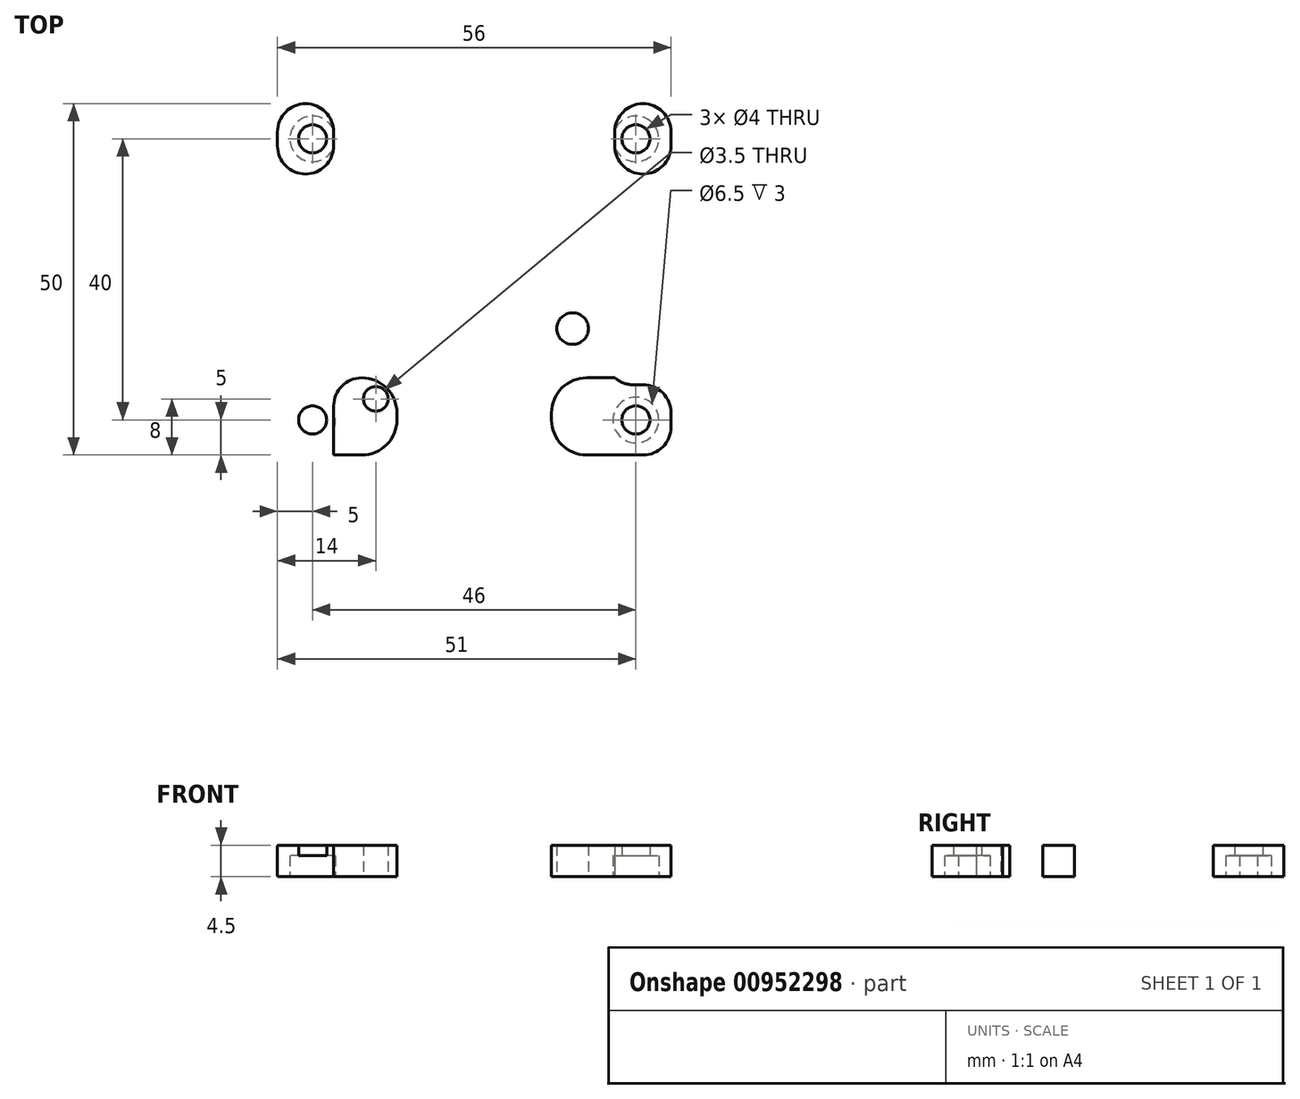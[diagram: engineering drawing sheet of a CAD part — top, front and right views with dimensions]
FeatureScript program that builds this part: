
annotation { "Feature Type Name" : "Feature", "Feature Type Description" : "" }
export const myFeature = defineFeature(function(context is Context, id is Id, definition is map)
    precondition{}
    {
        {
            var Q0;
            Q0=qCreatedBy(makeId("Top.planeOp"),FACE);
            var sketch = newSketch(context, id + "F0", { "sketchPlane" : qUnion([Q0])});
            skLineSegment(sketch, "E0.bottom", {"start": v(20, -27) * mm, "end": v(-20, -27) * mm});
            skLineSegment(sketch, "E0.top", {"start": v(20, 27) * mm, "end": v(-20, 27) * mm});
            skLineSegment(sketch, "E0.left", {"start": v(20, -27) * mm, "end": v(20, 27) * mm});
            skLineSegment(sketch, "E0.right", {"start": v(-20, -27) * mm, "end": v(-20, 27) * mm});
            skPoint(sketch, "E0.middle", {"position": v(0, 0) * mm});
            skCircle(sketch, "E1", {"center": v(0, 8.9) * mm, "radius": 6 * mm});
            skCircle(sketch, "E2", {"center": v(14, 20) * mm, "radius": 2.25 * mm});
            skCircle(sketch, "E3.MirrorC", {"center": v(-14, 20) * mm, "radius": 2.25 * mm});
            skCircle(sketch, "E4.MirrorC", {"center": v(14, -20) * mm, "radius": 2.25 * mm});
            skCircle(sketch, "E5.MirrorC", {"center": v(-14, -20) * mm, "radius": 2.25 * mm});
            skCircle(sketch, "E6", {"center": v(-14, -10) * mm, "radius": 1.75 * mm});
            skCircle(sketch, "E7.MirrorC", {"center": v(14, -10) * mm, "radius": 1.75 * mm});
            skLineSegment(sketch, "E8.bottom", {"start": v(-20, -27) * mm, "end": v(20, -27) * mm});
            skLineSegment(sketch, "E8.top", {"start": v(-20, -38) * mm, "end": v(-11, -38) * mm});
            skLineSegment(sketch, "E8.left", {"start": v(-20, -27) * mm, "end": v(-20, -38) * mm});
            skLineSegment(sketch, "E8.right", {"start": v(20, -27) * mm, "end": v(20, -38) * mm});
            skCircle(sketch, "E9", {"center": v(-14, -30) * mm, "radius": 1.75 * mm});
            skCircle(sketch, "E10.MirrorC", {"center": v(14, -30) * mm, "radius": 1.75 * mm});
            skLineSegment(sketch, "E11.MirrorCS", {"start": v(-28, 12) * mm, "end": v(-28, -38) * mm});
            skLineSegment(sketch, "E12.MirrorCS", {"start": v(-11, -38) * mm, "end": v(-28, -38) * mm});
            skLineSegment(sketch, "E13", {"start": v(-28, 12) * mm, "end": v(-20, 12) * mm});
            skLineSegment(sketch, "E14.left", {"start": v(-11, -38) * mm, "end": v(-11, -30) * mm});
            skLineSegment(sketch, "E14.right", {"start": v(11, -38) * mm, "end": v(11, -30) * mm});
            skLineSegment(sketch, "E15.top", {"start": v(-11, -27) * mm, "end": v(11, -27) * mm});
            skLineSegment(sketch, "E15.left", {"start": v(-11, -30) * mm, "end": v(-11, -27) * mm});
            skLineSegment(sketch, "E15.right", {"start": v(11, -30) * mm, "end": v(11, -27) * mm});
            skCircle(sketch, "E16", {"center": v(0, -15) * mm, "radius": 7.5 * mm});
            skLineSegment(sketch, "E17.MirrorCS", {"start": v(-28, 2) * mm, "end": v(-20, 2) * mm});
            skCircle(sketch, "E18.MirrorC", {"center": v(-23, 7) * mm, "radius": 2 * mm});
            skCircle(sketch, "E19.MirrorC", {"center": v(-23, -33) * mm, "radius": 2 * mm});
            skLineSegment(sketch, "E20", {"start": v(-28, -28) * mm, "end": v(-20, -28) * mm});
            skPoint(sketch, "E21.MirrorCS.start.orphan", {"position": v(-20, 27) * mm});
            skLineSegment(sketch, "E22.MirrorCS", {"start": v(28, 12) * mm, "end": v(20, 12) * mm});
            skCircle(sketch, "E23.MirrorC", {"center": v(23, 7) * mm, "radius": 2 * mm});
            skLineSegment(sketch, "E24.MirrorCS", {"start": v(28, 12) * mm, "end": v(28, -38) * mm});
            skLineSegment(sketch, "E25.MirrorCS", {"start": v(28, 2) * mm, "end": v(20, 2) * mm});
            skLineSegment(sketch, "E26.MirrorCS", {"start": v(28, -28) * mm, "end": v(20, -28) * mm});
            skLineSegment(sketch, "E27.MirrorCS", {"start": v(11, -38) * mm, "end": v(28, -38) * mm});
            skCircle(sketch, "E28.MirrorC", {"center": v(23, -33) * mm, "radius": 2 * mm});
            skLineSegment(sketch, "E29.trimOffspring", {"start": v(11, -38) * mm, "end": v(20, -38) * mm});
            skSolve(sketch);
        }
        {
            var Q0;
            Q0=makeQuery(id+"F0.imprint","IMPRINT",FACE,{"disambiguationData":[TD([[makeQuery(id+"F0.imprint","IMPRINT",EDGE,{"derivedFrom":sQuery(id+"F0.wireOp",EDGE,"EJkg02S6-5hP4-Ptk8-ohYH-sUQTjE6RF98o")}),-1.0]])]});
            var Q1;
            Q1=makeQuery(id+"F0.imprint","IMPRINT",FACE,{"disambiguationData":[TD([[makeQuery(id+"F0.imprint","IMPRINT",EDGE,{"derivedFrom":sQuery(id+"F0.wireOp",EDGE,"fef3ff0a-59c7-4115-b365-545473ce19e80.MirrorC")}),-1.0]])]});
            var Q2;
            Q2=makeQuery(id+"F0.imprint","IMPRINT",FACE,{"disambiguationData":[TD([[makeQuery(id+"F0.imprint","IMPRINT",EDGE,{"derivedFrom":sQuery(id+"F0.wireOp",EDGE,"83bcec90-f7c3-4e6e-a305-b15cb3412ae00.MirrorC")}),1.0]])]});
            var Q3;
            {var subQ3=sQuery(id+"F0.wireOp",EDGE,"E8.bottom");Q3=makeQuery(id+"F0.imprint","IMPRINT",FACE,{"disambiguationData":[TD([[makeQuery(id+"F0.imprint","IMPRINT",EDGE,{"derivedFrom":subQ3}),-1.0]])]});}
            var Q4;
            Q4=makeQuery(id+"F0.imprint","IMPRINT",FACE,{"disambiguationData":[TD([[makeQuery(id+"F0.imprint","IMPRINT",EDGE,{"derivedFrom":sQuery(id+"F0.wireOp",EDGE,"E1")}),-1.0]])]});
            var Q5;
            {var subQ4=sQuery(id+"F0.wireOp",EDGE,"cf22b2a7-dd2e-4435-8f2e-39b4c899264f0.MirrorCS");Q5=makeQuery(id+"F0.imprint","IMPRINT",FACE,{"disambiguationData":[TD([[makeQuery(id+"F0.imprint","IMPRINT",EDGE,{"derivedFrom":subQ4}),-1.0]])]});}
            var Q6;
            {var subQ1=sQuery(id+"F0.wireOp",EDGE,"E0.top");Q6=makeQuery(id+"F0.imprint","IMPRINT",FACE,{"disambiguationData":[TD([[makeQuery(id+"F0.imprint","IMPRINT",EDGE,{"derivedFrom":subQ1}),1.0]])]});}
            var Q7;
            Q7=makeQuery(id+"F0.imprint","IMPRINT",FACE,{"disambiguationData":[TD([[makeQuery(id+"F0.imprint","IMPRINT",EDGE,{"derivedFrom":sQuery(id+"F0.wireOp",EDGE,"E9")}),-1.0]])]});
            var Q8;
            Q8=makeQuery(id+"F0.imprint","IMPRINT",FACE,{"disambiguationData":[TD([[makeQuery(id+"F0.imprint","IMPRINT",EDGE,{"derivedFrom":sQuery(id+"F0.wireOp",EDGE,"E10.MirrorC")}),1.0]])]});
            var Q9;
            {var subQ6=sQuery(id+"F0.wireOp",EDGE,"E14.left");Q9=makeQuery(id+"F0.imprint","IMPRINT",FACE,{"disambiguationData":[TD([[makeQuery(id+"F0.imprint","IMPRINT",EDGE,{"derivedFrom":subQ6}),1.0]])]});}
            var Q10;
            {var subQ10=sQuery(id+"F0.wireOp",EDGE,"E14.right");Q10=makeQuery(id+"F0.imprint","IMPRINT",FACE,{"disambiguationData":[TD([[makeQuery(id+"F0.imprint","IMPRINT",EDGE,{"derivedFrom":subQ10}),-1.0]])]});}
            var Q11;
            Q11=makeQuery(id+"F0.imprint","IMPRINT",FACE,{"disambiguationData":[TD([[makeQuery(id+"F0.imprint","IMPRINT",EDGE,{"derivedFrom":sQuery(id+"F0.wireOp",EDGE,"E4.MirrorC")}),1.0]])]});
            var Q12;
            {var subQ0=sQuery(id+"F0.wireOp",EDGE,"ed930464-472b-4d13-baf5-ac3ff7af2bd40.MirrorCS");Q12=makeQuery(id+"F0.imprint","IMPRINT",FACE,{"disambiguationData":[TD([[makeQuery(id+"F0.imprint","IMPRINT",EDGE,{"derivedFrom":subQ0}),1.0]])]});}
            var Q13;
            {var subQ1=sQuery(id+"F0.wireOp",EDGE,"E13");Q13=makeQuery(id+"F0.imprint","IMPRINT",FACE,{"disambiguationData":[TD([[makeQuery(id+"F0.imprint","IMPRINT",EDGE,{"derivedFrom":subQ1}),-1.0]])]});}
            var Q14;
            {var subQ1=sQuery(id+"F0.wireOp",EDGE,"D3Rt8Xrc-2Lu0-yaOw-90uC-Wp8pwz9pcPP1.top");Q14=makeQuery(id+"F0.imprint","IMPRINT",FACE,{"disambiguationData":[TD([[makeQuery(id+"F0.imprint","IMPRINT",EDGE,{"derivedFrom":subQ1}),1.0]])]});}
            var Q15;
            {var subQ1=sQuery(id+"F0.wireOp",EDGE,"E22.MirrorCS");Q15=makeQuery(id+"F0.imprint","IMPRINT",FACE,{"disambiguationData":[TD([[makeQuery(id+"F0.imprint","IMPRINT",EDGE,{"derivedFrom":subQ1}),1.0]])]});}
            var Q16;
            {var subQ1=sQuery(id+"F0.wireOp",EDGE,"E26.MirrorCS");Q16=makeQuery(id+"F0.imprint","IMPRINT",FACE,{"disambiguationData":[TD([[makeQuery(id+"F0.imprint","IMPRINT",EDGE,{"derivedFrom":subQ1}),1.0]])]});}
            var Q17;
            Q17=makeQuery(id+"F0.imprint","IMPRINT",FACE,{"disambiguationData":[TD([[makeQuery(id+"F0.imprint","IMPRINT",EDGE,{"derivedFrom":sQuery(id+"F0.wireOp",EDGE,"E19.MirrorC")}),1.0]])]});
            extrude(context, id + "F1", {"entities" : qUnion([Q0, Q1, Q2, Q3, Q4, Q5, Q6, Q7, Q8, Q9, Q10, Q11, Q12, Q13, Q14, Q15, Q16, Q17]), "depth" : 4.5 * mm, "offsetDistance" : 25 * mm});
        }
        {
            var Q0;
            Q0=makeQuery(id+"F1.opExtrude","CAP_FACE",FACE,{"disambiguationData":[OSD([sQuery(id+"F0.wireOp",EDGE,"E0.bottom"),sQuery(id+"F0.wireOp",EDGE,"E0.top"),sQuery(id+"F0.wireOp",EDGE,"E0.left"),sQuery(id+"F0.wireOp",EDGE,"E0.right"),sQuery(id+"F0.wireOp",EDGE,"E1"),sQuery(id+"F0.wireOp",EDGE,"E2"),sQuery(id+"F0.wireOp",EDGE,"E3.MirrorC"),sQuery(id+"F0.wireOp",EDGE,"E4.MirrorC"),sQuery(id+"F0.wireOp",EDGE,"E5.MirrorC")])],"isStart":false});
            var sketch = newSketch(context, id + "F2", { "sketchPlane" : qUnion([Q0])});
            skCircle(sketch, "E30", {"center": v(0, 20.9) * mm, "radius": 1.3 * mm});
            skCircle(sketch, "E31.1.0", {"center": v(-8.49, 17.39) * mm, "radius": 1.3 * mm});
            skCircle(sketch, "E31.2.0", {"center": v(-12, 8.9) * mm, "radius": 1.3 * mm});
            skCircle(sketch, "E31.3.0", {"center": v(-8.49, 0.41) * mm, "radius": 1.3 * mm});
            skCircle(sketch, "E31.4.0", {"center": v(0, -3.1) * mm, "radius": 1.3 * mm});
            skCircle(sketch, "E31.5.0", {"center": v(8.49, 0.41) * mm, "radius": 1.3 * mm});
            skCircle(sketch, "E31.6.0", {"center": v(12, 8.9) * mm, "radius": 1.3 * mm});
            skCircle(sketch, "E31.7.0", {"center": v(8.49, 17.39) * mm, "radius": 1.3 * mm});
            skPoint(sketch, "E31.center", {"position": v(0, 8.9) * mm});
            skSolve(sketch);
        }
        {
            var Q0;
            Q0 = qSketchRegion(id + "F2", true);
            extrude(context, id + "F3", {"entities" : qUnion([Q0]), "operationType" : NewBodyOperationType.REMOVE, "oppositeDirection" : true, "depth" : 25 * mm, "offsetDistance" : 25 * mm});
        }
        {
            var Q0;
            Q0=makeQuery(id+"F1.opExtrude","CAP_FACE",FACE,{"disambiguationData":[OSD([sQuery(id+"F0.wireOp",EDGE,"E0.bottom"),sQuery(id+"F0.wireOp",EDGE,"E0.top"),sQuery(id+"F0.wireOp",EDGE,"E0.left"),sQuery(id+"F0.wireOp",EDGE,"E0.right"),sQuery(id+"F0.wireOp",EDGE,"E1"),sQuery(id+"F0.wireOp",EDGE,"E2"),sQuery(id+"F0.wireOp",EDGE,"E3.MirrorC"),sQuery(id+"F0.wireOp",EDGE,"E4.MirrorC"),sQuery(id+"F0.wireOp",EDGE,"E5.MirrorC"),sQuery(id+"F0.wireOp",EDGE,"E6"),sQuery(id+"F0.wireOp",EDGE,"E7.MirrorC")])],"isStart":false});
            var sketch = newSketch(context, id + "F4", { "sketchPlane" : qUnion([Q0])});
            skCircle(sketch, "E32", {"center": v(0, 8.9) * mm, "radius": 9.25 * mm});
            skSolve(sketch);
        }
        {
            var Q0;
            Q0=makeQuery(id+"F4.imprint","IMPRINT",FACE,{"disambiguationData":[TD([[makeQuery(id+"F4.imprint","IMPRINT",EDGE,{"derivedFrom":sQuery(id+"F4.wireOp",EDGE,"E32")}),1.0]])]});
            extrude(context, id + "F5", {"entities" : qUnion([Q0]), "operationType" : NewBodyOperationType.REMOVE, "oppositeDirection" : true, "depth" : 3 * mm, "offsetDistance" : 25 * mm});
        }
        {
            var Q0;
            Q0=makeQuery(id+"F1.opExtrude","SWEPT_EDGE",EDGE,{"disambiguationData":[OSD([sQuery(id+"F0.wireOp",EDGE,"D3Rt8Xrc-2Lu0-yaOw-90uC-Wp8pwz9pcPP1.bottom"),sQuery(id+"F0.wireOp",EDGE,"D3Rt8Xrc-2Lu0-yaOw-90uC-Wp8pwz9pcPP1.right")])]});
            var Q1;
            Q1=makeQuery(id+"F1.opExtrude","SWEPT_EDGE",EDGE,{"disambiguationData":[OSD([sQuery(id+"F0.wireOp",EDGE,"E21.MirrorCS"),sQuery(id+"F0.wireOp",EDGE,"E11.MirrorCS")])]});
            var Q2;
            Q2=makeQuery(id+"F1.opExtrude","SWEPT_EDGE",EDGE,{"disambiguationData":[OSD([sQuery(id+"F0.wireOp",EDGE,"E11.MirrorCS"),sQuery(id+"F0.wireOp",EDGE,"E12.MirrorCS")])]});
            var Q3;
            Q3=makeQuery(id+"F1.opExtrude","SWEPT_EDGE",EDGE,{"disambiguationData":[OSD([sQuery(id+"F0.wireOp",EDGE,"D3Rt8Xrc-2Lu0-yaOw-90uC-Wp8pwz9pcPP1.top"),sQuery(id+"F0.wireOp",EDGE,"D3Rt8Xrc-2Lu0-yaOw-90uC-Wp8pwz9pcPP1.right")])]});
            var Q4;
            Q4=makeQuery(id+"F1.opExtrude","SWEPT_EDGE",EDGE,{"disambiguationData":[OSD([sQuery(id+"F0.wireOp",EDGE,"E22.MirrorCS"),sQuery(id+"F0.wireOp",EDGE,"E24.MirrorCS")])]});
            var Q5;
            Q5=makeQuery(id+"F1.opExtrude","SWEPT_EDGE",EDGE,{"disambiguationData":[OSD([sQuery(id+"F0.wireOp",EDGE,"E24.MirrorCS"),sQuery(id+"F0.wireOp",EDGE,"E26.MirrorCS")])]});
            var Q6;
            Q6=makeQuery(id+"F1.opExtrude","SWEPT_EDGE",EDGE,{"disambiguationData":[OSD([sQuery(id+"F0.wireOp",EDGE,"E24.MirrorCS"),sQuery(id+"F0.wireOp",EDGE,"E27.MirrorCS")])]});
            var Q7;
            Q7=makeQuery(id+"F1.opExtrude","SWEPT_EDGE",EDGE,{"disambiguationData":[OSD([sQuery(id+"F0.wireOp",EDGE,"E0.right"),sQuery(id+"F0.wireOp",EDGE,"E17.MirrorCS")])]});
            var Q8;
            Q8=makeQuery(id+"F1.opExtrude","SWEPT_EDGE",EDGE,{"disambiguationData":[OSD([sQuery(id+"F0.wireOp",EDGE,"E0.right"),sQuery(id+"F0.wireOp",EDGE,"E8.bottom"),sQuery(id+"F0.wireOp",EDGE,"E8.left"),sQuery(id+"F0.wireOp",EDGE,"E20")])]});
            var Q9;
            Q9=makeQuery(id+"F1.opExtrude","SWEPT_EDGE",EDGE,{"disambiguationData":[OSD([sQuery(id+"F0.wireOp",EDGE,"E24.MirrorCS"),sQuery(id+"F0.wireOp",EDGE,"E25.MirrorCS")])]});
            var Q10;
            Q10=makeQuery(id+"F1.opExtrude","SWEPT_EDGE",EDGE,{"disambiguationData":[OSD([sQuery(id+"F0.wireOp",EDGE,"D3Rt8Xrc-2Lu0-yaOw-90uC-Wp8pwz9pcPP1.left"),sQuery(id+"F0.wireOp",EDGE,"E25.MirrorCS")])]});
            var Q11;
            Q11=makeQuery(id+"F1.opExtrude","SWEPT_EDGE",EDGE,{"disambiguationData":[OSD([sQuery(id+"F0.wireOp",EDGE,"D3Rt8Xrc-2Lu0-yaOw-90uC-Wp8pwz9pcPP1.left"),sQuery(id+"F0.wireOp",EDGE,"E22.MirrorCS")])]});
            var Q12;
            Q12=makeQuery(id+"F1.opExtrude","SWEPT_EDGE",EDGE,{"disambiguationData":[OSD([sQuery(id+"F0.wireOp",EDGE,"E8.bottom"),sQuery(id+"F0.wireOp",EDGE,"D3Rt8Xrc-2Lu0-yaOw-90uC-Wp8pwz9pcPP1.left"),sQuery(id+"F0.wireOp",EDGE,"E26.MirrorCS")])]});
            var Q13;
            Q13=makeQuery(id+"F1.opExtrude","SWEPT_EDGE",EDGE,{"disambiguationData":[OSD([sQuery(id+"F0.wireOp",EDGE,"E0.top"),sQuery(id+"F0.wireOp",EDGE,"D3Rt8Xrc-2Lu0-yaOw-90uC-Wp8pwz9pcPP1.left")])]});
            var Q14;
            Q14=makeQuery(id+"F1.opExtrude","SWEPT_EDGE",EDGE,{"disambiguationData":[OSD([sQuery(id+"F0.wireOp",EDGE,"E0.top"),sQuery(id+"F0.wireOp",EDGE,"E0.right")])]});
            var Q15;
            Q15=makeQuery(id+"F1.opExtrude","SWEPT_EDGE",EDGE,{"disambiguationData":[OSD([sQuery(id+"F0.wireOp",EDGE,"E0.right"),sQuery(id+"F0.wireOp",EDGE,"E13")])]});
            fillet(context, id + "F6", {"entities" : qUnion([Q0, Q1, Q2, Q3, Q4, Q5, Q6, Q7, Q8, Q9, Q10, Q11, Q12, Q13, Q14, Q15]), "radius" : 4 * mm, "tangentPropagation" : true, "defaultsChanged" : true, "vertexSettings" : [], "allowEdgeOverflow" : false});
        }
        {
            var Q0;
            Q0=makeQuery(id+"F1.opExtrude","CAP_FACE",FACE,{"disambiguationData":[OSD([sQuery(id+"F0.wireOp",EDGE,"E0.top"),sQuery(id+"F0.wireOp",EDGE,"E0.right"),sQuery(id+"F0.wireOp",EDGE,"E1"),sQuery(id+"F0.wireOp",EDGE,"E2"),sQuery(id+"F0.wireOp",EDGE,"E3.MirrorC"),sQuery(id+"F0.wireOp",EDGE,"E4.MirrorC"),sQuery(id+"F0.wireOp",EDGE,"E5.MirrorC"),sQuery(id+"F0.wireOp",EDGE,"E6"),sQuery(id+"F0.wireOp",EDGE,"E7.MirrorC"),sQuery(id+"F0.wireOp",EDGE,"E8.top"),sQuery(id+"F0.wireOp",EDGE,"E8.left"),sQuery(id+"F0.wireOp",EDGE,"E9"),sQuery(id+"F0.wireOp",EDGE,"E10.MirrorC"),sQuery(id+"F0.wireOp",EDGE,"D3Rt8Xrc-2Lu0-yaOw-90uC-Wp8pwz9pcPP1.left"),sQuery(id+"F0.wireOp",EDGE,"D3Rt8Xrc-2Lu0-yaOw-90uC-Wp8pwz9pcPP1.right"),sQuery(id+"F0.wireOp",EDGE,"E11.MirrorCS"),sQuery(id+"F0.wireOp",EDGE,"54b7e0aa-d997-4b68-9832-fdfdaffa90230.MirrorC"),sQuery(id+"F0.wireOp",EDGE,"E13"),sQuery(id+"F0.wireOp",EDGE,"ed930464-472b-4d13-baf5-ac3ff7af2bd40.MirrorCS"),sQuery(id+"F0.wireOp",EDGE,"19901839-3c46-41ca-8788-d41f0cd191730.MirrorCS"),sQuery(id+"F0.wireOp",EDGE,"cf22b2a7-dd2e-4435-8f2e-39b4c899264f0.MirrorCS"),sQuery(id+"F0.wireOp",EDGE,"p6VOYzIL-zI26-ACcN-cJwr-jFxnP6v1cvRD"),sQuery(id+"F0.wireOp",EDGE,"0cb7f256-9682-4ea5-b6a4-6d857fac44b80.MirrorCS"),sQuery(id+"F0.wireOp",EDGE,"f13d7c97-2755-4da3-855d-ca262ee3f6ac0.MirrorCS"),sQuery(id+"F0.wireOp",EDGE,"8a3ca074-0cdb-465c-b89e-58528f1b61150.MirrorCS"),sQuery(id+"F0.wireOp",EDGE,"E14.bottom"),sQuery(id+"F0.wireOp",EDGE,"E16"),sQuery(id+"F0.wireOp",EDGE,"2b5bb6d6-d79d-4220-9a91-da7e43a042570.MirrorC"),sQuery(id+"F0.wireOp",EDGE,"406bb23d-c7b4-408d-befd-0ce35687cc040.MirrorC"),sQuery(id+"F0.wireOp",EDGE,"37f19dd3-176b-4e02-9f00-8a2677ea555e0.MirrorC")])],"isStart":true});
            var sketch = newSketch(context, id + "F7", { "sketchPlane" : qUnion([Q0])});
            skCircle(sketch, "E33", {"center": v(23, -7) * mm, "radius": 3.25 * mm});
            skCircle(sketch, "E34", {"center": v(23, 33) * mm, "radius": 3.25 * mm});
            skCircle(sketch, "E35.MirrorC", {"center": v(-23, -7) * mm, "radius": 3.25 * mm});
            skCircle(sketch, "E36.MirrorC", {"center": v(-23, 33) * mm, "radius": 3.25 * mm});
            skSolve(sketch);
        }
        {
            var Q0;
            Q0 = qSketchRegion(id + "F7", true);
            extrude(context, id + "F8", {"entities" : qUnion([Q0]), "operationType" : NewBodyOperationType.REMOVE, "oppositeDirection" : true, "depth" : 3 * mm, "offsetDistance" : 25 * mm});
        }
        {
            var Q0;
            Q0=makeQuery(id+"F1.opExtrude","SWEPT_EDGE",EDGE,{"disambiguationData":[OSD([sQuery(id+"F0.wireOp",EDGE,"E8.bottom"),sQuery(id+"F0.wireOp",EDGE,"E15.top"),sQuery(id+"F0.wireOp",EDGE,"E15.left")])]});
            var Q1;
            Q1=makeQuery(id+"F1.opExtrude","SWEPT_EDGE",EDGE,{"disambiguationData":[OSD([sQuery(id+"F0.wireOp",EDGE,"E8.top"),sQuery(id+"F0.wireOp",EDGE,"E14.bottom"),sQuery(id+"F0.wireOp",EDGE,"E14.left")])]});
            var Q2;
            Q2=makeQuery(id+"F1.opExtrude","SWEPT_EDGE",EDGE,{"disambiguationData":[OSD([sQuery(id+"F0.wireOp",EDGE,"E8.bottom"),sQuery(id+"F0.wireOp",EDGE,"E15.top"),sQuery(id+"F0.wireOp",EDGE,"E15.right")])]});
            var Q3;
            Q3=makeQuery(id+"F1.opExtrude","SWEPT_EDGE",EDGE,{"disambiguationData":[OSD([sQuery(id+"F0.wireOp",EDGE,"E8.top"),sQuery(id+"F0.wireOp",EDGE,"E14.bottom"),sQuery(id+"F0.wireOp",EDGE,"E14.right")])]});
            fillet(context, id + "F9", {"entities" : qUnion([Q0, Q1, Q2, Q3]), "tangentPropagation" : true, "radius" : 5 * mm, "defaultsChanged" : false, "vertexSettings" : [], "allowEdgeOverflow" : false});
        }
        {
            var Q0;
            Q0=makeQuery(id+"F1.opExtrude","CAP_FACE",FACE,{"disambiguationData":[OSD([sQuery(id+"F0.wireOp",EDGE,"E0.top"),sQuery(id+"F0.wireOp",EDGE,"E0.right"),sQuery(id+"F0.wireOp",EDGE,"E1"),sQuery(id+"F0.wireOp",EDGE,"E2"),sQuery(id+"F0.wireOp",EDGE,"E3.MirrorC"),sQuery(id+"F0.wireOp",EDGE,"E4.MirrorC"),sQuery(id+"F0.wireOp",EDGE,"E5.MirrorC"),sQuery(id+"F0.wireOp",EDGE,"E6"),sQuery(id+"F0.wireOp",EDGE,"E7.MirrorC"),sQuery(id+"F0.wireOp",EDGE,"E8.top"),sQuery(id+"F0.wireOp",EDGE,"E9"),sQuery(id+"F0.wireOp",EDGE,"E10.MirrorC"),sQuery(id+"F0.wireOp",EDGE,"D3Rt8Xrc-2Lu0-yaOw-90uC-Wp8pwz9pcPP1.left"),sQuery(id+"F0.wireOp",EDGE,"E11.MirrorCS"),sQuery(id+"F0.wireOp",EDGE,"E12.MirrorCS"),sQuery(id+"F0.wireOp",EDGE,"E13"),sQuery(id+"F0.wireOp",EDGE,"E14.bottom"),sQuery(id+"F0.wireOp",EDGE,"E16"),sQuery(id+"F0.wireOp",EDGE,"E17.MirrorCS"),sQuery(id+"F0.wireOp",EDGE,"E18.MirrorC"),sQuery(id+"F0.wireOp",EDGE,"E19.MirrorC"),sQuery(id+"F0.wireOp",EDGE,"E20"),sQuery(id+"F0.wireOp",EDGE,"E22.MirrorCS"),sQuery(id+"F0.wireOp",EDGE,"E23.MirrorC"),sQuery(id+"F0.wireOp",EDGE,"E24.MirrorCS"),sQuery(id+"F0.wireOp",EDGE,"E25.MirrorCS"),sQuery(id+"F0.wireOp",EDGE,"E26.MirrorCS"),sQuery(id+"F0.wireOp",EDGE,"E27.MirrorCS"),sQuery(id+"F0.wireOp",EDGE,"E28.MirrorC")])],"isStart":true});
            var Q1;
            Q1=makeQuery(id+"F1.opExtrude","CAP_FACE",FACE,{"disambiguationData":[OSD([sQuery(id+"F0.wireOp",EDGE,"E0.top"),sQuery(id+"F0.wireOp",EDGE,"E0.right"),sQuery(id+"F0.wireOp",EDGE,"E1"),sQuery(id+"F0.wireOp",EDGE,"E2"),sQuery(id+"F0.wireOp",EDGE,"E3.MirrorC"),sQuery(id+"F0.wireOp",EDGE,"E4.MirrorC"),sQuery(id+"F0.wireOp",EDGE,"E5.MirrorC"),sQuery(id+"F0.wireOp",EDGE,"E6"),sQuery(id+"F0.wireOp",EDGE,"E7.MirrorC"),sQuery(id+"F0.wireOp",EDGE,"E8.top"),sQuery(id+"F0.wireOp",EDGE,"E9"),sQuery(id+"F0.wireOp",EDGE,"E10.MirrorC"),sQuery(id+"F0.wireOp",EDGE,"D3Rt8Xrc-2Lu0-yaOw-90uC-Wp8pwz9pcPP1.left"),sQuery(id+"F0.wireOp",EDGE,"E11.MirrorCS"),sQuery(id+"F0.wireOp",EDGE,"E12.MirrorCS"),sQuery(id+"F0.wireOp",EDGE,"E13"),sQuery(id+"F0.wireOp",EDGE,"E14.bottom"),sQuery(id+"F0.wireOp",EDGE,"E16"),sQuery(id+"F0.wireOp",EDGE,"E17.MirrorCS"),sQuery(id+"F0.wireOp",EDGE,"E18.MirrorC"),sQuery(id+"F0.wireOp",EDGE,"E19.MirrorC"),sQuery(id+"F0.wireOp",EDGE,"E20"),sQuery(id+"F0.wireOp",EDGE,"E22.MirrorCS"),sQuery(id+"F0.wireOp",EDGE,"E23.MirrorC"),sQuery(id+"F0.wireOp",EDGE,"E24.MirrorCS"),sQuery(id+"F0.wireOp",EDGE,"E25.MirrorCS"),sQuery(id+"F0.wireOp",EDGE,"E26.MirrorCS"),sQuery(id+"F0.wireOp",EDGE,"E27.MirrorCS"),sQuery(id+"F0.wireOp",EDGE,"E28.MirrorC")])],"isStart":false});
            var Q2;
            Q2=makeQuery(id+"F5.boolean.opBoolean","COPY",FACE,{"derivedFrom":makeQuery(id+"F5.opExtrude","CAP_FACE",FACE,{"disambiguationData":[OSD([sQuery(id+"F0.wireOp",EDGE,"E1"),sQuery(id+"F4.wireOp",EDGE,"E32")])],"isStart":false})});
            fillet(context, id + "F10", {"entities" : qUnion([Q0, Q1, Q2]), "tangentPropagation" : true, "radius" : 0.2 * mm, "defaultsChanged" : false, "vertexSettings" : [], "allowEdgeOverflow" : false});
        }
    });
